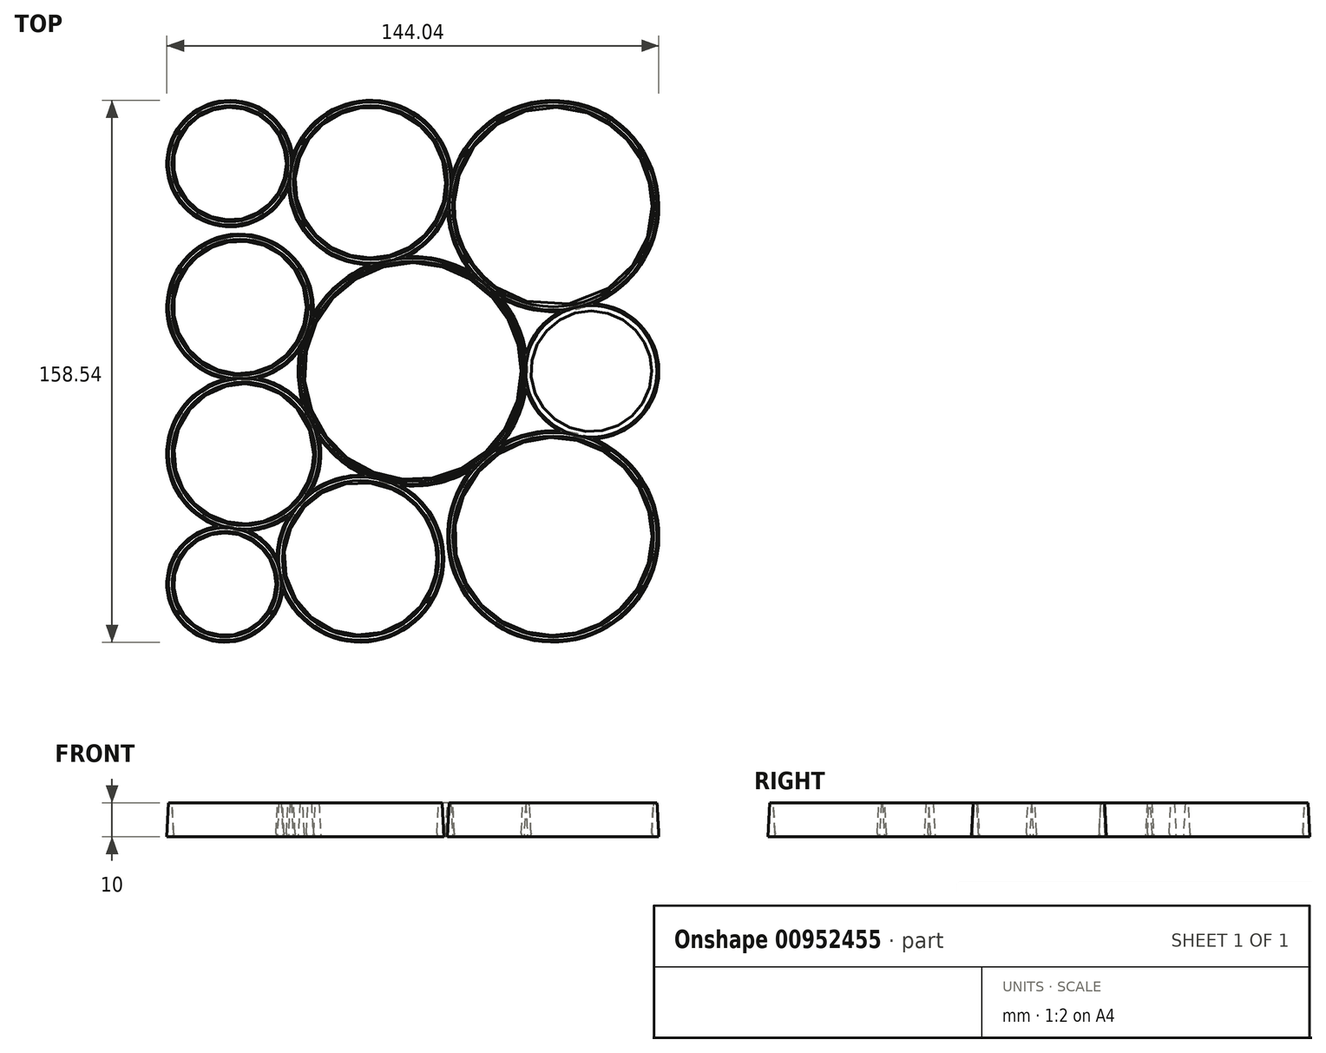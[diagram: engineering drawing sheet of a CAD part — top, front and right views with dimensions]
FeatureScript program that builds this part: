
annotation { "Feature Type Name" : "Feature", "Feature Type Description" : "" }
export const myFeature = defineFeature(function(context is Context, id is Id, definition is map)
    precondition{}
    {
        {
            var Q0;
            Q0=qCreatedBy(makeId("Top.planeOp"),FACE);
            var sketch = newSketch(context, id + "F0", { "sketchPlane" : qUnion([Q0])});
            skLineSegment(sketch, "E0.bottom", {"start": v(-71.5, 78.75) * mm, "end": v(71.5, 78.75) * mm});
            skLineSegment(sketch, "E0.top", {"start": v(-71.5, -78.75) * mm, "end": v(71.5, -78.75) * mm});
            skLineSegment(sketch, "E0.left", {"start": v(-71.5, 78.75) * mm, "end": v(-71.5, -78.75) * mm});
            skLineSegment(sketch, "E0.right", {"start": v(71.5, 78.75) * mm, "end": v(71.5, -78.75) * mm});
            skPoint(sketch, "E0.middle", {"position": v(0, 0) * mm});
            skCircle(sketch, "E1", {"center": v(0, 0) * mm, "radius": 33.05 * mm});
            skCircle(sketch, "E2", {"center": v(41.1, 48.35) * mm, "radius": 30.4 * mm});
            skCircle(sketch, "E3", {"center": v(52.28, 0) * mm, "radius": 19.22 * mm});
            skCircle(sketch, "E4", {"center": v(41.1, -48.35) * mm, "radius": 30.4 * mm});
            skCircle(sketch, "E5", {"center": v(-15.33, -54.85) * mm, "radius": 23.9 * mm});
            skCircle(sketch, "E6", {"center": v(-49.48, -24.17) * mm, "radius": 22.02 * mm});
            skCircle(sketch, "E7", {"center": v(-50.6, 18.73) * mm, "radius": 20.9 * mm});
            skCircle(sketch, "E8", {"center": v(-53.53, 60.78) * mm, "radius": 17.97 * mm});
            skCircle(sketch, "E9", {"center": v(-55.02, -62.27) * mm, "radius": 16.48 * mm});
            skCircle(sketch, "E10", {"center": v(-12.4, 55.21) * mm, "radius": 23.54 * mm});
            skCircle(sketch, "E11", {"center": v(-53.53, 60.78) * mm, "radius": 16.97 * mm});
            skCircle(sketch, "E12", {"center": v(-12.4, 55.21) * mm, "radius": 22.54 * mm});
            skCircle(sketch, "E13", {"center": v(41.1, 48.35) * mm, "radius": 29.46 * mm});
            skCircle(sketch, "E14", {"center": v(0, 0) * mm, "radius": 32.22 * mm});
            skCircle(sketch, "E15", {"center": v(-50.6, 18.73) * mm, "radius": 19.9 * mm});
            skCircle(sketch, "E16", {"center": v(-49.48, -24.17) * mm, "radius": 20.96 * mm});
            skCircle(sketch, "E17", {"center": v(-55.02, -62.27) * mm, "radius": 15.44 * mm});
            skCircle(sketch, "E18", {"center": v(-15.33, -54.85) * mm, "radius": 22.84 * mm});
            skCircle(sketch, "E19", {"center": v(52.28, 0) * mm, "radius": 18.14 * mm});
            skCircle(sketch, "E20", {"center": v(41.1, -48.35) * mm, "radius": 29.4 * mm});
            skSolve(sketch);
        }
        {
            var Q0;
            Q0=makeQuery(id+"F0.imprint","IMPRINT",FACE,{"disambiguationData":[TD([[makeQuery(id+"F0.imprint","IMPRINT",EDGE,{"derivedFrom":sQuery(id+"F0.wireOp",EDGE,"E11")}),-1.0]])]});
            var Q1;
            Q1=makeQuery(id+"F0.imprint","IMPRINT",FACE,{"disambiguationData":[TD([[makeQuery(id+"F0.imprint","IMPRINT",EDGE,{"derivedFrom":sQuery(id+"F0.wireOp",EDGE,"E15")}),-1.0]])]});
            var Q2;
            Q2=makeQuery(id+"F0.imprint","IMPRINT",FACE,{"disambiguationData":[TD([[makeQuery(id+"F0.imprint","IMPRINT",EDGE,{"derivedFrom":sQuery(id+"F0.wireOp",EDGE,"E12")}),-1.0]])]});
            var Q3;
            Q3=makeQuery(id+"F0.imprint","IMPRINT",FACE,{"disambiguationData":[TD([[makeQuery(id+"F0.imprint","IMPRINT",EDGE,{"derivedFrom":sQuery(id+"F0.wireOp",EDGE,"E14")}),-1.0]])]});
            var Q4;
            Q4=makeQuery(id+"F0.imprint","IMPRINT",FACE,{"disambiguationData":[TD([[makeQuery(id+"F0.imprint","IMPRINT",EDGE,{"derivedFrom":sQuery(id+"F0.wireOp",EDGE,"E13")}),-1.0]])]});
            var Q5;
            Q5=makeQuery(id+"F0.imprint","IMPRINT",FACE,{"disambiguationData":[TD([[makeQuery(id+"F0.imprint","IMPRINT",EDGE,{"derivedFrom":sQuery(id+"F0.wireOp",EDGE,"E19")}),-1.0]])]});
            var Q6;
            Q6=makeQuery(id+"F0.imprint","IMPRINT",FACE,{"disambiguationData":[TD([[makeQuery(id+"F0.imprint","IMPRINT",EDGE,{"derivedFrom":sQuery(id+"F0.wireOp",EDGE,"E20")}),-1.0]])]});
            var Q7;
            Q7=makeQuery(id+"F0.imprint","IMPRINT",FACE,{"disambiguationData":[TD([[makeQuery(id+"F0.imprint","IMPRINT",EDGE,{"derivedFrom":sQuery(id+"F0.wireOp",EDGE,"E18")}),-1.0]])]});
            var Q8;
            Q8=makeQuery(id+"F0.imprint","IMPRINT",FACE,{"disambiguationData":[TD([[makeQuery(id+"F0.imprint","IMPRINT",EDGE,{"derivedFrom":sQuery(id+"F0.wireOp",EDGE,"E17")}),-1.0]])]});
            var Q9;
            Q9=makeQuery(id+"F0.imprint","IMPRINT",FACE,{"disambiguationData":[TD([[makeQuery(id+"F0.imprint","IMPRINT",EDGE,{"derivedFrom":sQuery(id+"F0.wireOp",EDGE,"E16")}),-1.0]])]});
            extrude(context, id + "F1", {"entities" : qUnion([Q0, Q1, Q2, Q3, Q4, Q5, Q6, Q7, Q8, Q9]), "oppositeDirection" : true, "depth" : 10 * mm, "offsetDistance" : 25 * mm, "hasDraft" : true, "draftAngle" : 3 * degree});
        }
        {
            var Q0;
            Q0=makeQuery(id+"F1.opExtrude","CAP_EDGE",EDGE,{"disambiguationData":[OSD([sQuery(id+"F0.wireOp",EDGE,"E13")])],"isStart":false});
            var Q1;
            Q1=makeQuery(id+"F1.opExtrude","SWEPT_FACE",FACE,{"disambiguationData":[OSD([sQuery(id+"F0.wireOp",EDGE,"E19")])]});
            var Q2;
            Q2=makeQuery(id+"F1.opExtrude","CAP_EDGE",EDGE,{"disambiguationData":[OSD([sQuery(id+"F0.wireOp",EDGE,"E20")])],"isStart":false});
            var Q3;
            Q3=makeQuery(id+"F1.opExtrude","CAP_EDGE",EDGE,{"disambiguationData":[OSD([sQuery(id+"F0.wireOp",EDGE,"E14")])],"isStart":false});
            var Q4;
            Q4=makeQuery(id+"F1.opExtrude","CAP_EDGE",EDGE,{"disambiguationData":[OSD([sQuery(id+"F0.wireOp",EDGE,"E12")])],"isStart":false});
            var Q5;
            Q5=makeQuery(id+"F1.opExtrude","CAP_EDGE",EDGE,{"disambiguationData":[OSD([sQuery(id+"F0.wireOp",EDGE,"E11")])],"isStart":false});
            var Q6;
            Q6=makeQuery(id+"F1.opExtrude","CAP_EDGE",EDGE,{"disambiguationData":[OSD([sQuery(id+"F0.wireOp",EDGE,"E15")])],"isStart":false});
            var Q7;
            Q7=makeQuery(id+"F1.opExtrude","CAP_EDGE",EDGE,{"disambiguationData":[OSD([sQuery(id+"F0.wireOp",EDGE,"E16")])],"isStart":false});
            var Q8;
            Q8=makeQuery(id+"F1.opExtrude","CAP_EDGE",EDGE,{"disambiguationData":[OSD([sQuery(id+"F0.wireOp",EDGE,"E17")])],"isStart":false});
            var Q9;
            Q9=makeQuery(id+"F1.opExtrude","CAP_EDGE",EDGE,{"disambiguationData":[OSD([sQuery(id+"F0.wireOp",EDGE,"E18")])],"isStart":false});
            fillet(context, id + "F2", {"entities" : qUnion([Q0, Q1, Q2, Q3, Q4, Q5, Q6, Q7, Q8, Q9]), "radius" : 1 * mm, "allowEdgeOverflow" : false});
        }
    });
